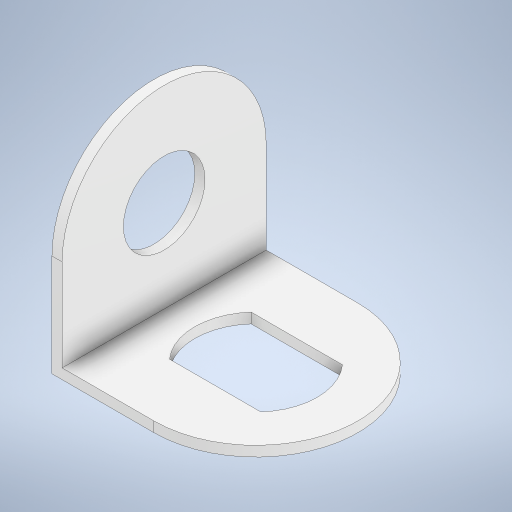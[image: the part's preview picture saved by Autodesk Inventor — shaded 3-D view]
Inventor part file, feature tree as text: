
AUTODESK INVENTOR PART (.ipt)
format: ipt  version: 2024 (Build 280153000, 153)  size: 339,456 bytes
history: native  units: mm
features: extrude x6, sketch x6, pattern_linear x2, other x1
ambient origin geometry x8: Origin, YZ Plane, XZ Plane, XY Plane, X Axis, Y Axis, Z Axis, Center Point
bodies: Body1 (feature_tree)
feature tree (15):
  other  "Těleso1"
  extrude  "Vysunutí1"  Depth=0.5mm
  extrude  "Vysunutí2"  Depth=0.5mm
  pattern_linear  "Obdélníkové pole1"  Spacing1=10.0mm  [1 undecoded]
  extrude  "Vysunutí4"  Depth=10.0mm
  extrude  "Vysunutí5"  Depth=10.0mm TaperAngle=0.0deg
  pattern_linear  "Obdélníkové pole3"  Spacing1=6.0mm  [1 undecoded]
  extrude  "Vysunutí6"  Depth=5.0mm
  extrude  "Vysunutí7"  Depth=5.0mm
  sketch  "Náčrt1"
  sketch  "Náčrt2"
  sketch  "Náčrt4"
  sketch  "Náčrt5"
  sketch  "Náčrt6"
  sketch  "Náčrt7"
note: 2 required parameter values undecoded (feature->parameter linkage not recoverable at this tier; creation-order binding heuristic only, values carry confidence <= 0.55)
